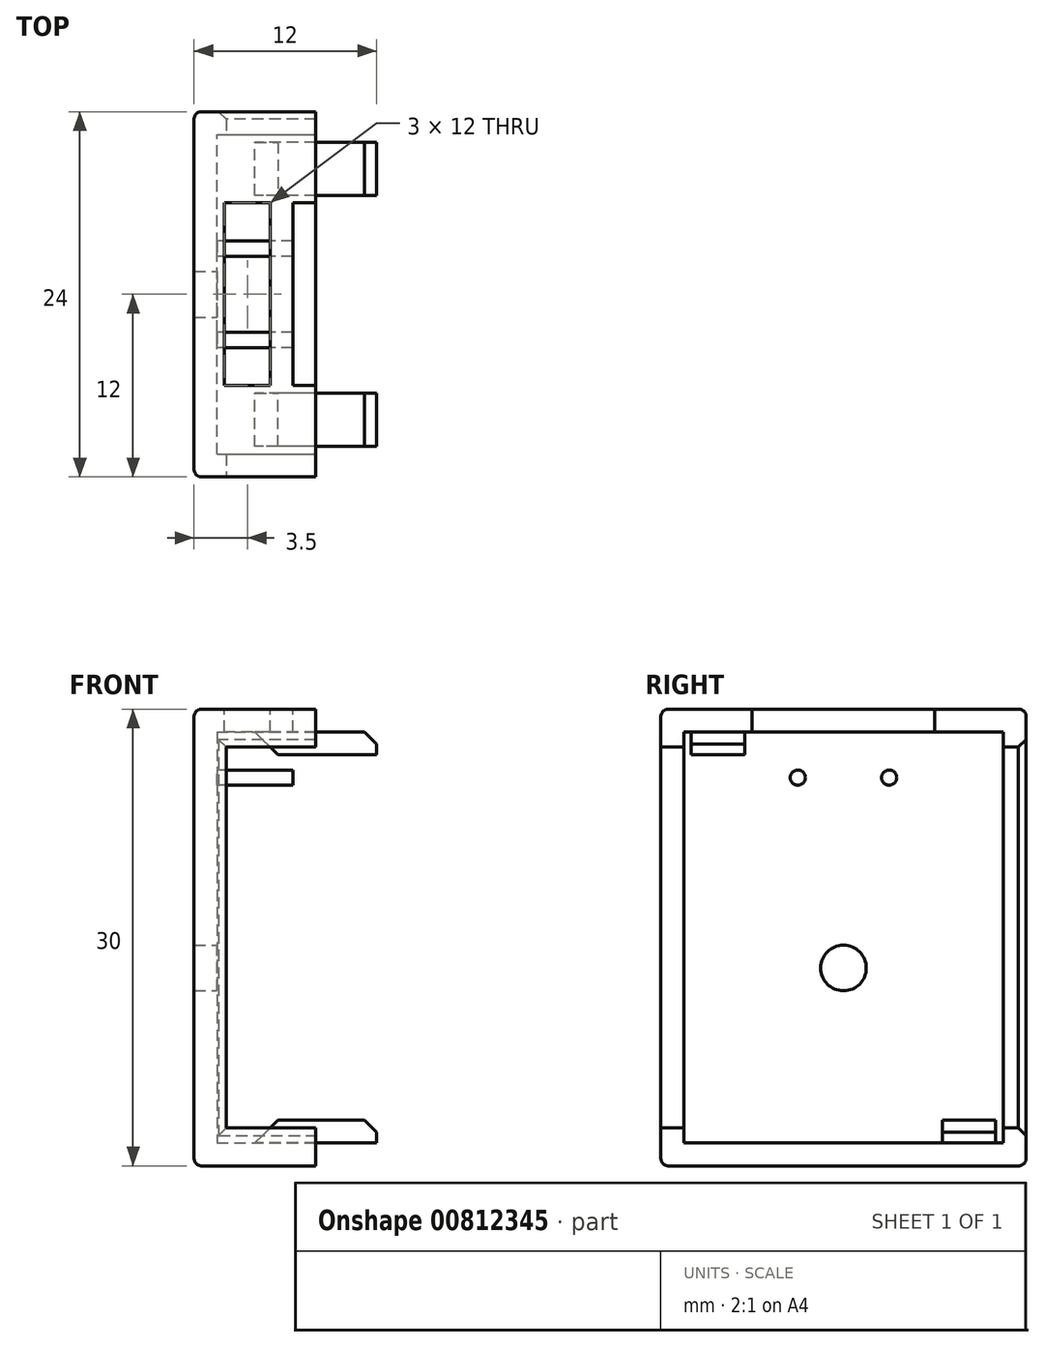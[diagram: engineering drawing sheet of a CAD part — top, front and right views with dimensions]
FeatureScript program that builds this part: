
annotation { "Feature Type Name" : "Feature", "Feature Type Description" : "" }
export const myFeature = defineFeature(function(context is Context, id is Id, definition is map)
    precondition{}
    {
        {
            var Q0;
            Q0=qCreatedBy(makeId("Right.planeOp"),FACE);
            var sketch = newSketch(context, id + "F0", { "sketchPlane" : qUnion([Q0])});
            skPoint(sketch, "E0", {"position": v(40.6, 0) * mm});
            skPoint(sketch, "E1", {"position": v(0, -40.6) * mm});
            skSolve(sketch);
        }
        {
            var Q0;
            Q0=qCreatedBy(makeId("Right.planeOp"),FACE);
            var sketch = newSketch(context, id + "F1", { "sketchPlane" : qUnion([Q0])});
            skLineSegment(sketch, "E2.bottom", {"start": v(-22, 0) * mm, "end": v(2, 0) * mm});
            skLineSegment(sketch, "E2.top", {"start": v(-22, -30) * mm, "end": v(2, -30) * mm});
            skLineSegment(sketch, "E2.left", {"start": v(-22, 0) * mm, "end": v(-22, -30) * mm});
            skLineSegment(sketch, "E2.right", {"start": v(2, 0) * mm, "end": v(2, -30) * mm});
            skSolve(sketch);
        }
        {
            var Q0;
            Q0 = qSketchRegion(id + "F1", true);
            extrude(context, id + "F2", {"entities" : qUnion([Q0]), "oppositeDirection" : true, "depth" : 8 * mm, "offsetDistance" : 25 * mm});
        }
        {
            var Q0;
            Q0=makeQuery(id+"F2.opExtrude","CAP_FACE",FACE,{"disambiguationData":[OSD([sQuery(id+"F1.wireOp",EDGE,"E2.bottom"),sQuery(id+"F1.wireOp",EDGE,"E2.top"),sQuery(id+"F1.wireOp",EDGE,"E2.left"),sQuery(id+"F1.wireOp",EDGE,"E2.right")])],"isStart":true});
            shell(context, id + "F3", {"entities" : qUnion([Q0]), "thickness" : 1.5 * mm});
        }
        {
            var Q0;
            Q0=qCreatedBy(makeId("Top.planeOp"),FACE);
            var sketch = newSketch(context, id + "F4", { "sketchPlane" : qUnion([Q0])});
            skLineSegment(sketch, "E3.bottom", {"start": v(-1.5, -16) * mm, "end": v(1.5, -16) * mm});
            skLineSegment(sketch, "E3.top", {"start": v(-1.5, -4) * mm, "end": v(1.5, -4) * mm});
            skLineSegment(sketch, "E3.left", {"start": v(-1.5, -16) * mm, "end": v(-1.5, -4) * mm});
            skLineSegment(sketch, "E3.right", {"start": v(1.5, -16) * mm, "end": v(1.5, -4) * mm});
            skPoint(sketch, "E4", {"position": v(0, -4) * mm});
            skLineSegment(sketch, "E5.1.0.0", {"start": v(-6, -16) * mm, "end": v(-6, -4) * mm});
            skLineSegment(sketch, "E5.1.0.1", {"start": v(-6, -4) * mm, "end": v(-3, -4) * mm});
            skLineSegment(sketch, "E5.1.0.2", {"start": v(-3, -16) * mm, "end": v(-3, -4) * mm});
            skLineSegment(sketch, "E5.1.0.3", {"start": v(-6, -16) * mm, "end": v(-3, -16) * mm});
            skLineSegment(sketch, "E5.direction1", {"start": v(-1.5, -16) * mm, "end": v(-6, -16) * mm, "construction": true});
            skSolve(sketch);
        }
        {
            var Q0;
            Q0 = qSketchRegion(id + "F4", true);
            extrude(context, id + "F5", {"entities" : qUnion([Q0]), "operationType" : NewBodyOperationType.REMOVE, "oppositeDirection" : true, "depth" : 5 * mm, "offsetDistance" : 25 * mm});
        }
        {
            var Q0;
            Q0=makeQuery(id+"F2.opExtrude","SWEPT_FACE",FACE,{"disambiguationData":[OSD([sQuery(id+"F1.wireOp",EDGE,"E2.left")])]});
            var sketch = newSketch(context, id + "F6", { "sketchPlane" : qUnion([Q0])});
            skLineSegment(sketch, "E6.bottom", {"start": v(-5.9, -2.5) * mm, "end": v(2.1, -2.5) * mm});
            skLineSegment(sketch, "E6.top", {"start": v(-5.9, -27.5) * mm, "end": v(2.1, -27.5) * mm});
            skLineSegment(sketch, "E6.left", {"start": v(-5.9, -2.5) * mm, "end": v(-5.9, -27.5) * mm});
            skLineSegment(sketch, "E6.right", {"start": v(2.1, -2.5) * mm, "end": v(2.1, -27.5) * mm});
            skSolve(sketch);
        }
        {
            var Q0;
            Q0 = qSketchRegion(id + "F6", true);
            extrude(context, id + "F7", {"entities" : qUnion([Q0]), "operationType" : NewBodyOperationType.REMOVE, "oppositeDirection" : true, "depth" : 30 * mm, "offsetDistance" : 25 * mm});
        }
        {
            var Q0;
            Q0=qCreatedBy(makeId("Right.planeOp"),FACE);
            var sketch = newSketch(context, id + "F8", { "sketchPlane" : qUnion([Q0])});
            skLineSegment(sketch, "E7.bottom", {"start": v(-20, -1.5) * mm, "end": v(-16.5, -1.5) * mm});
            skLineSegment(sketch, "E7.top", {"start": v(-20, -3) * mm, "end": v(-16.5, -3) * mm});
            skLineSegment(sketch, "E7.left", {"start": v(-20, -1.5) * mm, "end": v(-20, -3) * mm});
            skLineSegment(sketch, "E7.right", {"start": v(-16.5, -1.5) * mm, "end": v(-16.5, -3) * mm});
            skLineSegment(sketch, "E8.bottom", {"start": v(-3.5, -28.5) * mm, "end": v(0, -28.5) * mm});
            skLineSegment(sketch, "E8.top", {"start": v(-3.5, -27) * mm, "end": v(0, -27) * mm});
            skLineSegment(sketch, "E8.left", {"start": v(-3.5, -28.5) * mm, "end": v(-3.5, -27) * mm});
            skLineSegment(sketch, "E8.right", {"start": v(0, -28.5) * mm, "end": v(0, -27) * mm});
            skSolve(sketch);
        }
        {
            var Q0;
            Q0 = qSketchRegion(id + "F8", true);
            extrude(context, id + "F9", {"entities" : qUnion([Q0]), "operationType" : NewBodyOperationType.ADD, "depth" : 8 * mm, "offsetDistance" : 25 * mm, "symmetric" : true});
        }
        {
            var Q0;
            Q0=makeQuery(id+"F9.opExtrude","CAP_EDGE",EDGE,{"disambiguationData":[OSD([sQuery(id+"F8.wireOp",EDGE,"E7.bottom")])],"isStart":false});
            var Q1;
            Q1=makeQuery(id+"F9.opExtrude","CAP_EDGE",EDGE,{"disambiguationData":[OSD([sQuery(id+"F8.wireOp",EDGE,"E8.top")])],"isStart":false});
            chamfer(context, id + "F10", {"entities" : qUnion([Q0, Q1]), "width" : .8 * mm, "tangentPropagation" : true});
        }
        {
            var Q0;
            Q0=qCreatedBy(makeId("Right.planeOp"),FACE);
            var sketch = newSketch(context, id + "F11", { "sketchPlane" : qUnion([Q0])});
            skCircle(sketch, "E9", {"center": v(-10, -17) * mm, "radius": 1.5 * mm});
            skSolve(sketch);
        }
        {
            var Q0;
            Q0 = qSketchRegion(id + "F11", true);
            extrude(context, id + "F12", {"entities" : qUnion([Q0]), "operationType" : NewBodyOperationType.REMOVE, "oppositeDirection" : true, "depth" : 25 * mm, "offsetDistance" : 25 * mm});
        }
        {
            var Q0;
            Q0=makeQuery(id+"F2.opExtrude","SWEPT_EDGE",EDGE,{"disambiguationData":[OSD([sQuery(id+"F1.wireOp",EDGE,"E2.bottom"),sQuery(id+"F1.wireOp",EDGE,"E2.right")])]});
            var Q1;
            Q1=makeQuery(id+"F2.opExtrude","CAP_EDGE",EDGE,{"disambiguationData":[OSD([sQuery(id+"F1.wireOp",EDGE,"E2.right")])],"isStart":false});
            var Q2;
            Q2=makeQuery(id+"F2.opExtrude","SWEPT_EDGE",EDGE,{"disambiguationData":[OSD([sQuery(id+"F1.wireOp",EDGE,"E2.bottom"),sQuery(id+"F1.wireOp",EDGE,"E2.left")])]});
            var Q3;
            Q3=makeQuery(id+"F2.opExtrude","SWEPT_EDGE",EDGE,{"disambiguationData":[OSD([sQuery(id+"F1.wireOp",EDGE,"E2.top"),sQuery(id+"F1.wireOp",EDGE,"E2.left")])]});
            var Q4;
            Q4=makeQuery(id+"F2.opExtrude","SWEPT_EDGE",EDGE,{"disambiguationData":[OSD([sQuery(id+"F1.wireOp",EDGE,"E2.top"),sQuery(id+"F1.wireOp",EDGE,"E2.right")])]});
            var Q5;
            Q5=makeQuery(id+"F2.opExtrude","CAP_EDGE",EDGE,{"disambiguationData":[OSD([sQuery(id+"F1.wireOp",EDGE,"E2.bottom")])],"isStart":false});
            var Q6;
            Q6=makeQuery(id+"F2.opExtrude","CAP_EDGE",EDGE,{"disambiguationData":[OSD([sQuery(id+"F1.wireOp",EDGE,"E2.left")])],"isStart":false});
            var Q7;
            Q7=makeQuery(id+"F2.opExtrude","CAP_EDGE",EDGE,{"disambiguationData":[OSD([sQuery(id+"F1.wireOp",EDGE,"E2.top")])],"isStart":false});
            fillet(context, id + "F13", {"entities" : qUnion([Q0, Q1, Q2, Q3, Q4, Q5, Q6, Q7]), "tangentPropagation" : true, "radius" : .5 * mm, "defaultsChanged" : false, "vertexSettings" : [], "allowEdgeOverflow" : false});
        }
        {
            var Q0;
            Q0=makeQuery(id+"F7.boolean.opBoolean","INTERSECT",EDGE,{"derivedFrom":[makeQuery(id+"F2.opExtrude","SWEPT_FACE",FACE,{"disambiguationData":[OSD([sQuery(id+"F1.wireOp",EDGE,"E2.right")])]}),makeQuery(id+"F7.opExtrude","SWEPT_FACE",FACE,{"disambiguationData":[OSD([sQuery(id+"F6.wireOp",EDGE,"E6.left")])]})]});
            var Q1;
            Q1=makeQuery(id+"F7.boolean.opBoolean","INTERSECT",EDGE,{"derivedFrom":[makeQuery(id+"F2.opExtrude","SWEPT_FACE",FACE,{"disambiguationData":[OSD([sQuery(id+"F1.wireOp",EDGE,"E2.right")])]}),makeQuery(id+"F7.opExtrude","SWEPT_FACE",FACE,{"disambiguationData":[OSD([sQuery(id+"F6.wireOp",EDGE,"E6.bottom")])]})]});
            var Q2;
            Q2=makeQuery(id+"F7.boolean.opBoolean","INTERSECT",EDGE,{"derivedFrom":[makeQuery(id+"F2.opExtrude","SWEPT_FACE",FACE,{"disambiguationData":[OSD([sQuery(id+"F1.wireOp",EDGE,"E2.right")])]}),makeQuery(id+"F7.opExtrude","SWEPT_FACE",FACE,{"disambiguationData":[OSD([sQuery(id+"F6.wireOp",EDGE,"E6.top")])]})]});
            var Q3;
            Q3=makeQuery(id+"F7.boolean.opBoolean","COPY",EDGE,{"derivedFrom":makeQuery(id+"F7.opExtrude","CAP_EDGE",EDGE,{"disambiguationData":[OSD([sQuery(id+"F6.wireOp",EDGE,"E6.bottom")])],"isStart":true})});
            var Q4;
            Q4=makeQuery(id+"F7.boolean.opBoolean","COPY",EDGE,{"derivedFrom":makeQuery(id+"F7.opExtrude","CAP_EDGE",EDGE,{"disambiguationData":[OSD([sQuery(id+"F6.wireOp",EDGE,"E6.left")])],"isStart":true})});
            var Q5;
            Q5=makeQuery(id+"F7.boolean.opBoolean","COPY",EDGE,{"derivedFrom":makeQuery(id+"F7.opExtrude","CAP_EDGE",EDGE,{"disambiguationData":[OSD([sQuery(id+"F6.wireOp",EDGE,"E6.top")])],"isStart":true})});
            chamfer(context, id + "F14", {"entities" : qUnion([Q0, Q1, Q2, Q3, Q4, Q5]), "width" : .5 * mm, "tangentPropagation" : true});
        }
        {
            var Q0;
            Q0=makeQuery(id+"F3.opShell","OFFSET_FACE",FACE,{"disambiguationData":[OSD([sQuery(id+"F1.wireOp",EDGE,"E2.bottom"),sQuery(id+"F1.wireOp",EDGE,"E2.top"),sQuery(id+"F1.wireOp",EDGE,"E2.left"),sQuery(id+"F1.wireOp",EDGE,"E2.right")])]});
            var sketch = newSketch(context, id + "F15", { "sketchPlane" : qUnion([Q0])});
            skCircle(sketch, "E10", {"center": v(-13, -4.5) * mm, "radius": 0.5 * mm});
            skCircle(sketch, "E11", {"center": v(-7, -4.5) * mm, "radius": 0.5 * mm});
            skSolve(sketch);
        }
        {
            var Q0;
            Q0 = qSketchRegion(id + "F15", true);
            extrude(context, id + "F16", {"entities" : qUnion([Q0]), "operationType" : NewBodyOperationType.ADD, "depth" : 5 * mm, "offsetDistance" : 25 * mm});
        }
        {
            var Q0;
            Q0=makeQuery(id+"F9.opExtrude","CAP_EDGE",EDGE,{"disambiguationData":[OSD([sQuery(id+"F8.wireOp",EDGE,"E7.top")])],"isStart":true});
            var Q1;
            Q1=makeQuery(id+"F9.opExtrude","CAP_EDGE",EDGE,{"disambiguationData":[OSD([sQuery(id+"F8.wireOp",EDGE,"E8.top")])],"isStart":true});
            chamfer(context, id + "F17", {"entities" : qUnion([Q0, Q1]), "width" : 1.5 * mm, "tangentPropagation" : true});
        }
    });
